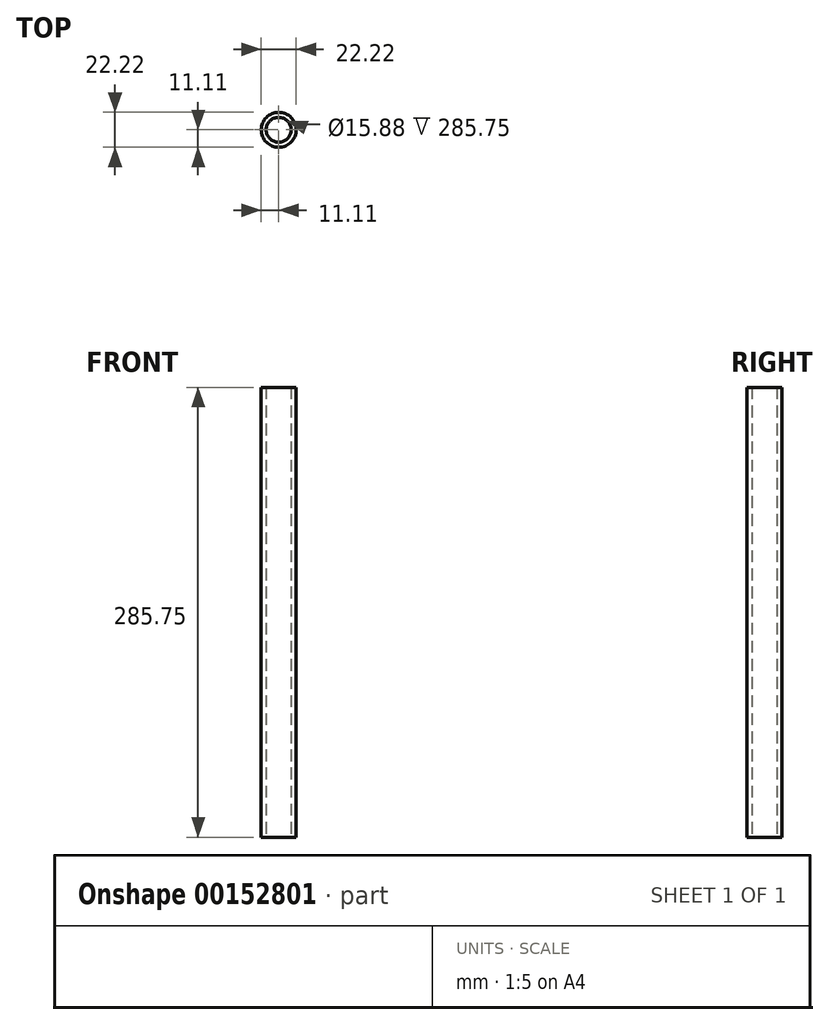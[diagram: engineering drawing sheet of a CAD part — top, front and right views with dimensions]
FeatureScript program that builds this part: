
annotation { "Feature Type Name" : "Feature", "Feature Type Description" : "" }
export const myFeature = defineFeature(function(context is Context, id is Id, definition is map)
    precondition{}
    {
        {
            var Q0;
            Q0=qCreatedBy(makeId("Top.planeOp"),FACE);
            var sketch = newSketch(context, id + "F0", { "sketchPlane" : qUnion([Q0])});
            skCircle(sketch, "E0", {"center": v(0, 0) * mm, "radius": 11.11 * mm});
            skCircle(sketch, "E1", {"center": v(0, 0) * mm, "radius": 7.94 * mm});
            skSolve(sketch);
        }
        {
            var Q0;
            Q0 = qSketchRegion(id + "F0", true);
            extrude(context, id + "F1", {"entities" : qUnion([Q0]), "depth" : 285.75 * mm});
        }
    });
